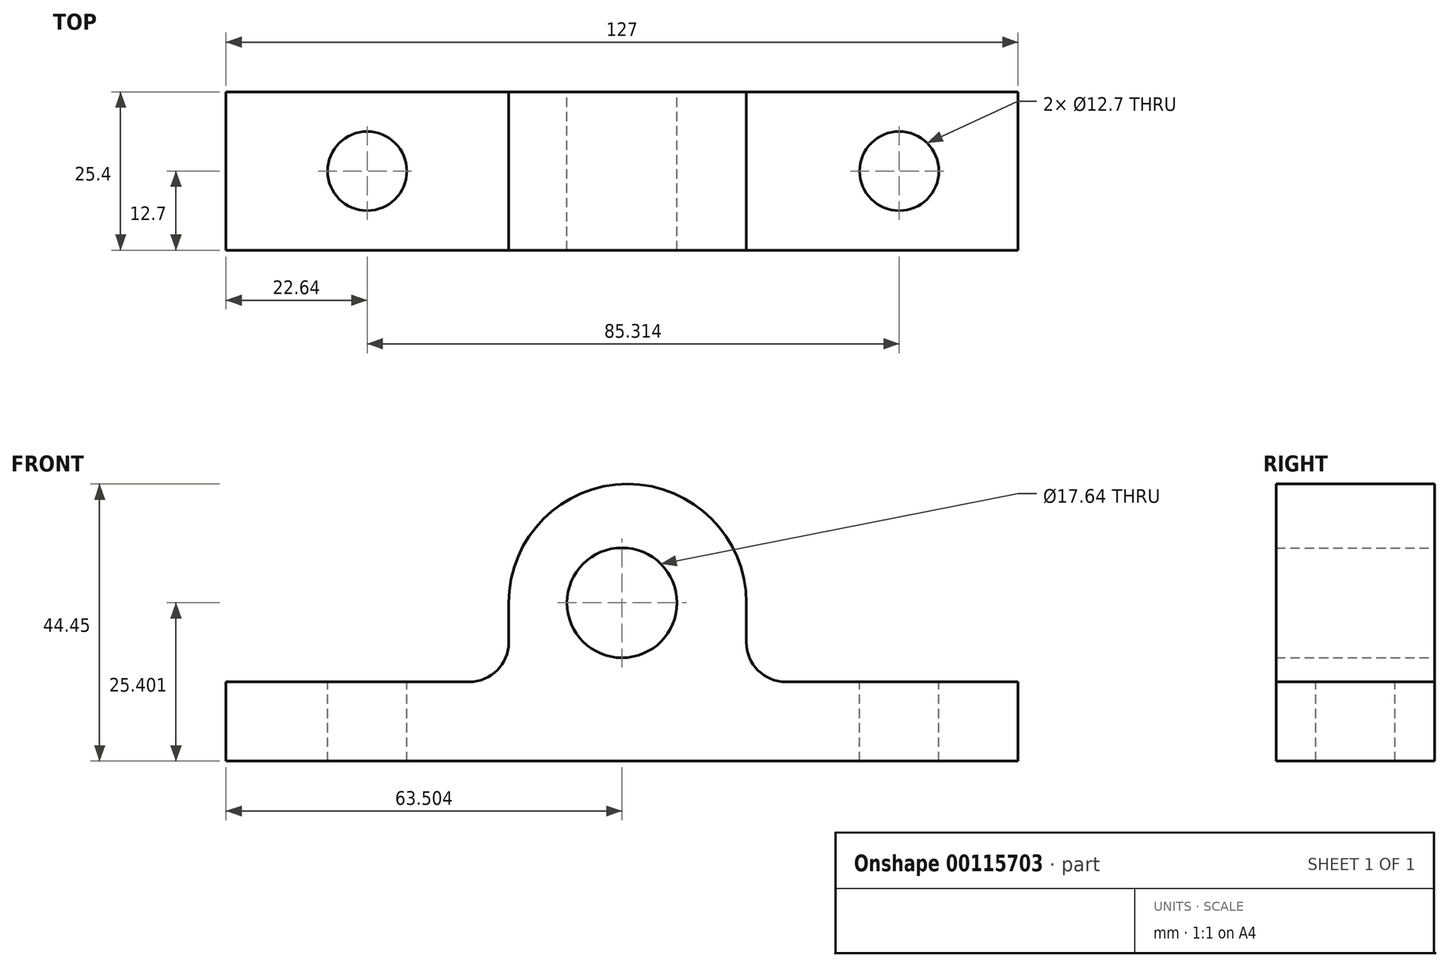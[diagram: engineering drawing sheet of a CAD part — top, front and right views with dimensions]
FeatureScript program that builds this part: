
annotation { "Feature Type Name" : "Feature", "Feature Type Description" : "" }
export const myFeature = defineFeature(function(context is Context, id is Id, definition is map)
    precondition{}
    {
        {
            var Q0;
            Q0=qCreatedBy(makeId("Front.planeOp"),FACE);
            var sketch = newSketch(context, id + "F0", { "sketchPlane" : qUnion([Q0])});
            skLineSegment(sketch, "E0.bottom", {"start": v(-22.64, 8.67) * mm, "end": v(16.35, 8.67) * mm});
            skLineSegment(sketch, "E0.top", {"start": v(-22.64, -4.03) * mm, "end": v(104.36, -4.03) * mm});
            skLineSegment(sketch, "E0.left", {"start": v(-22.64, 8.67) * mm, "end": v(-22.64, -4.03) * mm});
            skLineSegment(sketch, "E0.right", {"start": v(104.36, 8.67) * mm, "end": v(104.36, -4.03) * mm});
            skLineSegment(sketch, "E1", {"start": v(40.86, -4.03) * mm, "end": v(40.86, 21.37) * mm});
            skPoint(sketch, "E1.endSnap0", {"position": v(40.86, 8.67) * mm});
            skLineSegment(sketch, "E2", {"start": v(22.7, 15.02) * mm, "end": v(22.7, 21.37) * mm});
            skLineSegment(sketch, "E3", {"start": v(60.8, 15.02) * mm, "end": v(60.8, 21.37) * mm});
            skCircle(sketch, "E4", {"center": v(40.86, 21.37) * mm, "radius": 8.82 * mm});
            skPoint(sketch, "E5.newPointA", {"position": v(104.36, 8.67) * mm});
            skArc(sketch, "E5.filletArc", {"start": v(16.35, 8.67) * mm, "mid": v(20.84, 10.53) * mm, "end": v(22.7, 15.02) * mm});
            skLineSegment(sketch, "E6", {"start": v(104.36, 8.67) * mm, "end": v(67.15, 8.67) * mm});
            skPoint(sketch, "E7.visualSharp", {"position": v(60.8, 8.67) * mm});
            skArc(sketch, "E7.filletArc", {"start": v(60.8, 15.02) * mm, "mid": v(62.66, 10.53) * mm, "end": v(67.15, 8.67) * mm});
            skArc(sketch, "E8", {"start": v(60.8, 21.37) * mm, "mid": v(41.75, 40.42) * mm, "end": v(22.7, 21.37) * mm});
            skSolve(sketch);
        }
        {
            var Q0;
            Q0=makeQuery(id+"F0.imprint","IMPRINT",FACE,{"disambiguationData":[TD([[makeQuery(id+"F0.imprint","IMPRINT",EDGE,{"derivedFrom":sQuery(id+"F0.wireOp",EDGE,"E0.bottom")}),-1.0]])]});
            extrude(context, id + "F1", {"entities" : qUnion([Q0]), "depth" : 25.4 * mm});
        }
        {
            var Q0;
            Q0=makeQuery(id+"F1.opExtrude","SWEPT_FACE",FACE,{"disambiguationData":[OSD([sQuery(id+"F0.wireOp",EDGE,"E0.bottom")])]});
            var sketch = newSketch(context, id + "F2", { "sketchPlane" : qUnion([Q0])});
            skCircle(sketch, "E9", {"center": v(85.31, -12.7) * mm, "radius": 6.35 * mm});
            skPoint(sketch, "E9.centerSnap0", {"position": v(16.35, -12.7) * mm});
            skCircle(sketch, "E10", {"center": v(0, -12.7) * mm, "radius": 6.35 * mm});
            skSolve(sketch);
        }
        {
            var Q0;
            Q0=makeQuery(id+"F2.imprint","IMPRINT",FACE,{"disambiguationData":[TD([[makeQuery(id+"F2.imprint","IMPRINT",EDGE,{"derivedFrom":sQuery(id+"F2.wireOp",EDGE,"E10")}),1.0]])]});
            var Q1;
            Q1=makeQuery(id+"F2.imprint","IMPRINT",FACE,{"disambiguationData":[TD([[makeQuery(id+"F2.imprint","IMPRINT",EDGE,{"derivedFrom":sQuery(id+"F2.wireOp",EDGE,"E9")}),1.0]])]});
            extrude(context, id + "F3", {"entities" : qUnion([Q0, Q1]), "operationType" : NewBodyOperationType.REMOVE, "oppositeDirection" : true, "depth" : 25.4 * mm});
        }
    });
